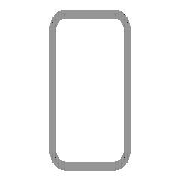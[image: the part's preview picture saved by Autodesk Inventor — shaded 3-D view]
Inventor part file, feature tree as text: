
AUTODESK INVENTOR PART (.ipt)
format: ipt  version: 2025 (Build 290162010, 162A)  size: 128,000 bytes
history: native  units: mm (DEFAULTED — no unit token found)
features: other x3, sketch x1, plane x1
ambient origin geometry x8: Origin, YZ Plane, XZ Plane, XY Plane, X Axis, Y Axis, Z Axis, Center Point
bodies: Solid1 (feature_tree), Body (feature_tree)
feature tree (5):
  other  "Driven Length"
  other  "Start plane"
  other  "End plane"
  sketch  "Sketch3"  dims[d3=2200.0mm d4=0.0mm d7=6.0mm d9=50.0mm d11=100.0mm d12=3.0mm d13=-0.0mm d14=2200.0mm d15=25.0mm d16=50.0mm d17=90.0deg d18=2200.0mm]
  plane  "Work Plane3"
